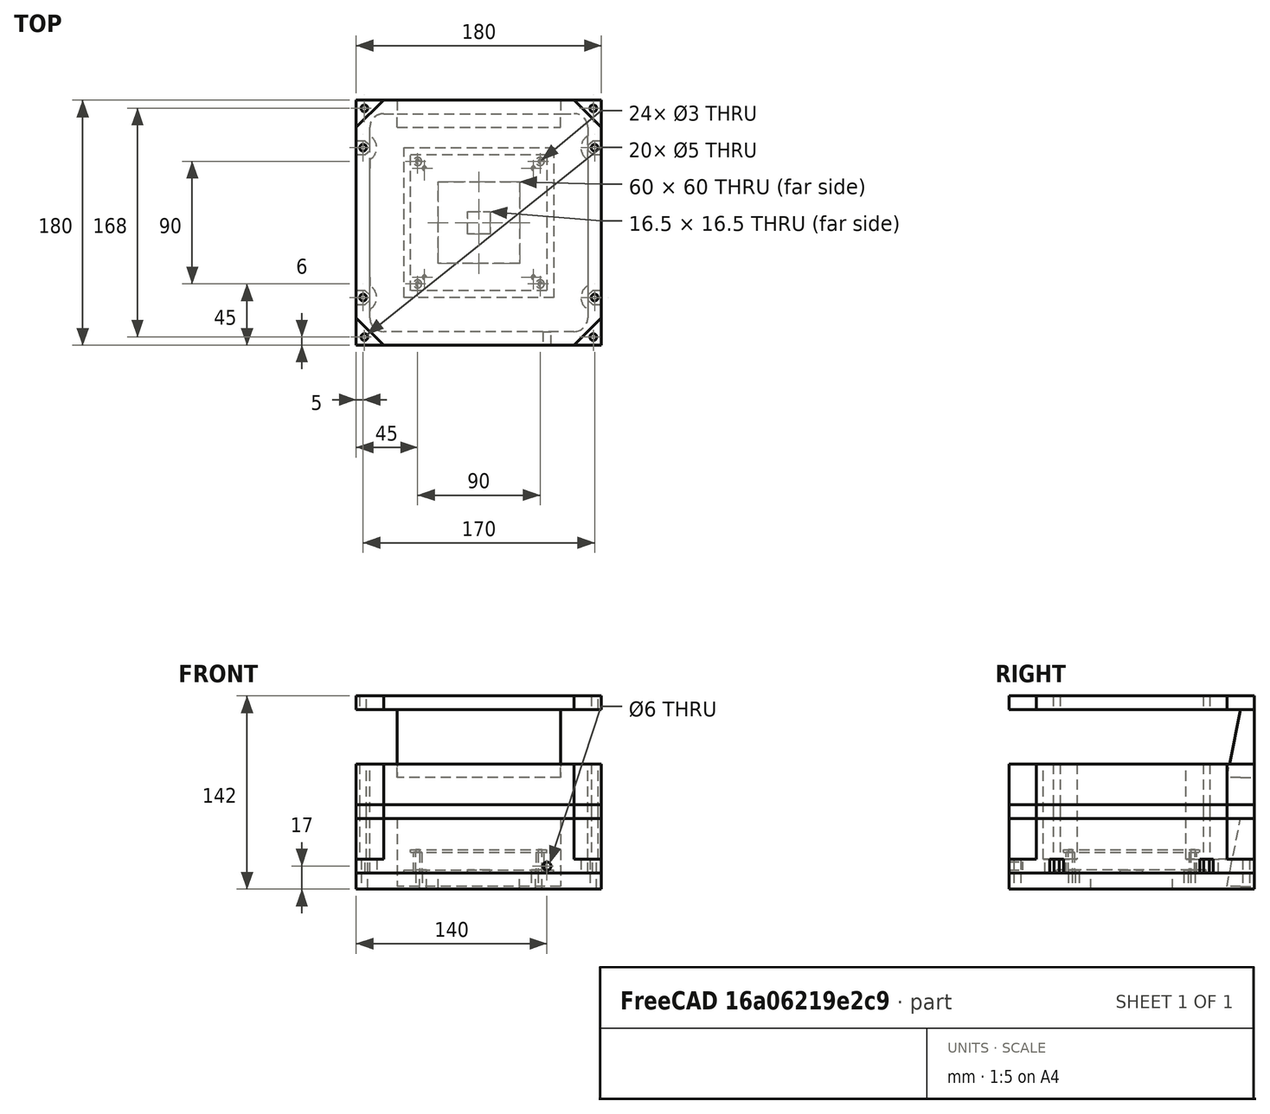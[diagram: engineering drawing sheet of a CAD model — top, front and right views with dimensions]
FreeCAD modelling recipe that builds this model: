
FCSTD DOCUMENT  (FreeCAD 0.19R24291 (Git))
Label: Cooling_skizze_1
License: All rights reserved
LicenseURL: http://en.wikipedia.org/wiki/All_rights_reserved
objects: TechDraw::DrawViewDimension×33, Sketcher::SketchObject×14, PartDesign::Pad×7, PartDesign::Pocket×6, PartDesign::Body×5, TechDraw::DrawViewAnnotation×4, PartDesign::PolarPattern×3, TechDraw::DrawSVGTemplate×3, TechDraw::DrawViewPart×3, TechDraw::DrawPage×3, PartDesign::AdditiveWedge×1, Part::Fuse×1
note: 51 computed .brp shape members not serialized (recipe doc carries the construction recipe); baked Part::Feature solids carry a one-line shape summary decoded from their .brp

FEATURE [Sketcher::SketchObject] Sketch  label="Sides"
  FullyConstrained = true
  MapMode = 2
  Support = -> [Sketch]
  sketch-geometry (31):
    g0: LineSegment StartX=-90 StartY=90 StartZ=0 EndX=90 EndY=90 EndZ=0
    g1: LineSegment StartX=90 StartY=90 StartZ=0 EndX=90 EndY=-90 EndZ=0
    g2: LineSegment StartX=90 StartY=-90 StartZ=0 EndX=-90 EndY=-90 EndZ=0
    g3: LineSegment StartX=-90 StartY=-90 StartZ=0 EndX=-90 EndY=90 EndZ=0
    g4: LineSegment StartX=-70 StartY=80 StartZ=0 EndX=70 EndY=80 EndZ=0
    g5: LineSegment StartX=80 StartY=70 StartZ=0 EndX=80 EndY=63.6603 EndZ=0
    g6: LineSegment StartX=70 StartY=-80 StartZ=0 EndX=-70 EndY=-80 EndZ=0
    g7: LineSegment StartX=-80 StartY=-70 StartZ=0 EndX=-80 EndY=-63.6603 EndZ=0
    g8: ArcOfCircle CenterX=70 CenterY=70 CenterZ=0 NormalX=0 NormalY=0 NormalZ=1 AngleXU=0 Radius=10 StartAngle=2.1e-15 EndAngle=1.5708
    g9: ArcOfCircle CenterX=70 CenterY=-70 CenterZ=0 NormalX=0 NormalY=0 NormalZ=1 AngleXU=0 Radius=10 StartAngle=4.71239 EndAngle=6.28319
    g10: GeomPoint X=80 Y=-80 Z=0
    g11: ArcOfCircle CenterX=-70 CenterY=-70 CenterZ=0 NormalX=0 NormalY=0 NormalZ=1 AngleXU=0 Radius=10 StartAngle=3.14159 EndAngle=4.71239
    g12: GeomPoint X=-80 Y=-80 Z=0
    g13: ArcOfCircle CenterX=-70 CenterY=70 CenterZ=0 NormalX=0 NormalY=0 NormalZ=1 AngleXU=0 Radius=10 StartAngle=1.5708 EndAngle=3.14212
    g14: GeomPoint X=-80 Y=80 Z=0
    g15: ArcOfCircle CenterX=-85 CenterY=55 CenterZ=0 NormalX=0 NormalY=0 NormalZ=1 AngleXU=0 Radius=10 StartAngle=5.23599 EndAngle=7.33038
    g16: LineSegment StartX=-80 StartY=63.6603 StartZ=0 EndX=-80 EndY=69.9948 EndZ=0
    g17: ArcOfCircle CenterX=85 CenterY=55 CenterZ=0 NormalX=0 NormalY=0 NormalZ=1 AngleXU=0 Radius=10 StartAngle=2.0944 EndAngle=4.18879
    g18: LineSegment StartX=80 StartY=46.3397 StartZ=0 EndX=80 EndY=-46.3397 EndZ=0
    g19: ArcOfCircle CenterX=-85 CenterY=-55 CenterZ=0 NormalX=0 NormalY=0 NormalZ=1 AngleXU=0 Radius=10 StartAngle=5.23599 EndAngle=7.33038
    g20: LineSegment StartX=-80 StartY=-46.3397 StartZ=0 EndX=-80 EndY=46.3397 EndZ=0
    g21: ArcOfCircle CenterX=85 CenterY=-55 CenterZ=0 NormalX=0 NormalY=0 NormalZ=1 AngleXU=0 Radius=10 StartAngle=2.0944 EndAngle=4.18879
    g22: LineSegment StartX=80 StartY=-63.6603 StartZ=0 EndX=80 EndY=-70 EndZ=0
    g23: Circle CenterX=-84 CenterY=84 CenterZ=0 NormalX=0 NormalY=0 NormalZ=1 AngleXU=0 Radius=2.5
    g24: Circle CenterX=84 CenterY=84 CenterZ=0 NormalX=0 NormalY=0 NormalZ=1 AngleXU=0 Radius=2.5
    g25: Circle CenterX=84 CenterY=-84 CenterZ=0 NormalX=0 NormalY=0 NormalZ=1 AngleXU=0 Radius=2.5
    g26: Circle CenterX=-84 CenterY=-84 CenterZ=0 NormalX=0 NormalY=0 NormalZ=1 AngleXU=0 Radius=2.5
    g27: Circle CenterX=-85 CenterY=55 CenterZ=0 NormalX=0 NormalY=0 NormalZ=1 AngleXU=0 Radius=2.5
    g28: Circle CenterX=-85 CenterY=-55 CenterZ=0 NormalX=0 NormalY=0 NormalZ=1 AngleXU=0 Radius=2.5
    g29: Circle CenterX=85 CenterY=-55 CenterZ=0 NormalX=0 NormalY=0 NormalZ=1 AngleXU=0 Radius=2.5
    g30: Circle CenterX=85 CenterY=55 CenterZ=0 NormalX=0 NormalY=0 NormalZ=1 AngleXU=0 Radius=2.5
  constraints (85):
    c: Coincident(g0,g1)
    c: Coincident(g1,g2)
    c: Coincident(g2,g3)
    c: Coincident(g3,g0)
    c: Horizontal(g0)
    c: Horizontal(g2)
    c: Vertical(g1)
    c: Vertical(g3)
    c: Horizontal(g6)
    c: Vertical(g7)
    c: Distance(g0) = 180
    c: Distance(g1) = 180
    c: Distance(g12,g10) = 160
    c: Distance(g14,g12) = 160
    c: Tangent(g5,g8) = 1.5708
    c: Tangent(g4,g8) = 1.5708
    c: PointOnObject(g10,g5)
    c: PointOnObject(g10,g6)
    c: Coincident(g22,g9) = 1.5708
    c: Tangent(g6,g9) = 1.5708
    c: PointOnObject(g12,g6)
    c: Tangent(g6,g11) = 1.5708
    c: Tangent(g7,g11) = 1.5708
    c: PointOnObject(g14,g7)
    c: PointOnObject(g14,g4)
    c: Coincident(g16,g13) = 1.5708
    c: Tangent(g4,g13) = 1.5708
    c: Radius(g11) = 10
    c: Coincident(g16,g15)
    c: Tangent(g7,g16)
    c: Coincident(g20,g15)
    c: Tangent(g5,g18)
    c: Coincident(g5,g17)
    c: Coincident(g20,g19)
    c: Tangent(g7,g20)
    c: Coincident(g7,g19)
    c: PointOnObject(g21,g18)
    c: Coincident(g18,g21)
    c: Coincident(g17,g18)
    c: Coincident(g21,g22)
    c: Radius(g9) = 10
    c: Radius(g19) = 10
    c: Radius(g15) = 10
    c: Diameter(g23) = 5  'Bohrung 1-b'
    c: DistanceY(g23,g0) = 6  'Versatz_y1-b'
    c: Diameter(g24) = 5  'Bohrung 2-b'
    c: DistanceX(g24,g0) = 6  'Versatz_x2-b'
    c: DistanceY(g24,g0) = 6  'Versatz_y2-b'
    c: DistanceX(g0,g23) = 6  'Versatz_x1-b'
    c: DistanceX(g8,g0) = 20
    c: DistanceY(g8,g0) = 20
    c: Diameter(g25) = 5  'Bohrung 3-b'
    c: DistanceX(g25,g1) = 6  'Versatz_x3-b'
    c: DistanceY(g1,g25) = 6  'Versatz_y3-b'
    c: Diameter(g26) = 5  'Bohrung 4-b'
    c: DistanceX(g2,g26) = 6  'Versatz_x4-b'
    c: DistanceY(g2,g26) = 6  'Versatz_y4-b'
    c: Coincident(g27,g15)
    c: Diameter(g27) = 5  'Bohrung 1-t'
    c: Coincident(g28,g19)
    c: Diameter(g28) = 5  'Bohrung 4-t'
    c: Coincident(g29,g21)
    c: Diameter(g29) = 5  'Bohrung 3-t'
    c: Coincident(g30,g17)
    c: Diameter(g30) = 5  'Bohrung 2-t'
    c: DistanceY(g15,g23) = 29  'Abstand 1b-t'
    c: DistanceX(g0,g15) = 5  'Versatz_1-t'
    c: Radius(g17) = 10
    c: DistanceY(g17,g24) = 29  'Abstand 2b-t'
    c: DistanceX(g17,g0) = 5  'Versatz_2-t'
    c: Radius(g21) = 10
    c: DistanceY(g25,g21) = 29  'Abstand 3b-t'
    c: DistanceX(g21,g1) = 5  'Versatz_3-t'
    c: DistanceY(g26,g19) = 29  'Abstand 4b-t'
    c: DistanceX(g2,g19) = 5  'Versatz_4-t'
    c: DistanceX(g0,g-1) = 90
    c: DistanceY(g-1,g0) = 90
    c: DistanceX(g-1,g10) = 80
    c: DistanceY(g10,g-1) = 80
    c: DistanceY(g10,g14) = 160
    c: DistanceX(g12,g4) = 150
    c: DistanceX(g4,g4) = 140
    c: Distance(g6) = 140
    c: DistanceY(g6,g9) = 10
    c: DistanceY(g13,g14) = 10
FEATURE [PartDesign::Pad] Pad  label="Bodypad"
  Direction = (1,1,1)
  Length = 80
  Length2 = 100
  Profile = -> Sketch
  Type = 0
FEATURE [Sketcher::SketchObject] Sketch001  label="Side-Cutout"
  FullyConstrained = true
  MapMode = 5
  Placement = pos=(0,90,0) rot=(0,0.707107,0.707107;3.14159rad)
  Support = -> [Pad]
  sketch-geometry (4):
    g0: LineSegment StartX=-60 StartY=80 StartZ=0 EndX=60 EndY=80 EndZ=0
    g1: LineSegment StartX=60 StartY=80 StartZ=0 EndX=60 EndY=0 EndZ=0
    g2: LineSegment StartX=60 StartY=0 StartZ=0 EndX=-60 EndY=0 EndZ=0
    g3: LineSegment StartX=-60 StartY=0 StartZ=0 EndX=-60 EndY=80 EndZ=0
  constraints (12):
    c: Coincident(g0,g1)
    c: Coincident(g1,g2)
    c: Coincident(g2,g3)
    c: Coincident(g3,g0)
    c: Horizontal(g0)
    c: Horizontal(g2)
    c: Vertical(g1)
    c: Vertical(g3)
    c: Distance(g0) = 120
    c: DistanceX(g0,g-1) = 60
    c: DistanceY(g-1,g0) = 80
    c: Distance(g1) = 80
FEATURE [PartDesign::Pocket] Pocket  label="Cutout-Side"
  BaseFeature = -> Pad
  Length = 11
  Length2 = 100
  Profile = -> Sketch001
  Type = 0
FEATURE [Sketcher::SketchObject] Sketch003  label="Cutdown B"
  FullyConstrained = true
  MapMode = 5
  Placement = pos=(0,0,80) rot=(0,0,1;0rad)
  sketch-geometry (3):
    g0: LineSegment StartX=-90 StartY=90 StartZ=0 EndX=-70 EndY=90 EndZ=0
    g1: LineSegment StartX=-90 StartY=70 StartZ=0 EndX=-90 EndY=90 EndZ=0
    g2: LineSegment StartX=-90 StartY=70 StartZ=0 EndX=-70 EndY=90 EndZ=0
  constraints (9):
    c: Coincident(g1,g0)
    c: Horizontal(g0)
    c: Vertical(g1)
    c: DistanceX(g0,g-1) = 90
    c: DistanceY(g-1,g0) = 90
    c: Distance(g0) = 20
    c: PointOnObject(g2,g0)
    c: Block(g2)
    c: Distance(g1) = 20
FEATURE [PartDesign::Pocket] Pocket002  label="Cut-Down B"
  BaseFeature = -> Pocket
  Length = 70
  Length2 = 100
  Profile = -> Sketch003
  Type = 0
FEATURE [PartDesign::PolarPattern] PolarPattern  label="PatternCutDownsB"
  Angle = 360
  Axis = -> Sketch003 [N_Axis]
  BaseFeature = -> Pocket002
  Occurrences = 4
  Originals = -> [Pocket002]
FEATURE [Sketcher::SketchObject] Sketch004  label="Cutdown T"
  FullyConstrained = true
  MapMode = 5
  Placement = pos=(0,0,0) rot=(1,0,0;3.14159rad)
  Support = -> [PolarPattern]
  sketch-geometry (24):
    g0: LineSegment StartX=-90 StartY=60 StartZ=0 EndX=-83.5 EndY=60 EndZ=0
    g1: LineSegment StartX=-80 StartY=57 StartZ=0 EndX=-80 EndY=53 EndZ=0
    g2: LineSegment StartX=-83.5 StartY=50 StartZ=0 EndX=-90 EndY=50 EndZ=0
    g3: LineSegment StartX=-90 StartY=50 StartZ=0 EndX=-90 EndY=60 EndZ=0
    g4: LineSegment StartX=83.5 StartY=60 StartZ=0 EndX=90 EndY=60 EndZ=0
    g5: LineSegment StartX=90 StartY=60 StartZ=0 EndX=90 EndY=50 EndZ=0
    g6: LineSegment StartX=90 StartY=50 StartZ=0 EndX=83.5 EndY=50 EndZ=0
    g7: LineSegment StartX=80 StartY=53 StartZ=0 EndX=80 EndY=57 EndZ=0
    g8: LineSegment StartX=83.5 StartY=-50 StartZ=0 EndX=90 EndY=-50 EndZ=0
    g9: LineSegment StartX=90 StartY=-50 StartZ=0 EndX=90 EndY=-60 EndZ=0
    g10: LineSegment StartX=90 StartY=-60 StartZ=0 EndX=83.5 EndY=-60 EndZ=0
    g11: LineSegment StartX=80 StartY=-57 StartZ=0 EndX=80 EndY=-53 EndZ=0
    g12: LineSegment StartX=-90 StartY=-50 StartZ=0 EndX=-83.5 EndY=-50 EndZ=0
    g13: LineSegment StartX=-80 StartY=-53 StartZ=0 EndX=-80 EndY=-57 EndZ=0
    g14: LineSegment StartX=-83.5 StartY=-60 StartZ=0 EndX=-90 EndY=-60 EndZ=0
    g15: LineSegment StartX=-90 StartY=-60 StartZ=0 EndX=-90 EndY=-50 EndZ=0
    g16: LineSegment StartX=-83.5 StartY=-50 StartZ=0 EndX=-80 EndY=-53 EndZ=0
    g17: LineSegment StartX=-83.5 StartY=-60 StartZ=0 EndX=-80 EndY=-57 EndZ=0
    g18: LineSegment StartX=-83.5 StartY=60 StartZ=0 EndX=-80 EndY=57 EndZ=0
    g19: LineSegment StartX=-80 StartY=53 StartZ=0 EndX=-83.5 EndY=50 EndZ=0
    g20: LineSegment StartX=83.5 StartY=-50 StartZ=0 EndX=80 EndY=-53 EndZ=0
    g21: LineSegment StartX=80 StartY=-57 StartZ=0 EndX=83.5 EndY=-60 EndZ=0
    g22: LineSegment StartX=83.5 StartY=60 StartZ=0 EndX=80 EndY=57 EndZ=0
    g23: LineSegment StartX=80 StartY=53 StartZ=0 EndX=83.5 EndY=50 EndZ=0
  constraints (72):
    c: Coincident(g2,g3)
    c: Coincident(g3,g0)
    c: Horizontal(g0)
    c: Horizontal(g2)
    c: Vertical(g1)
    c: Vertical(g3)
    c: Distance(g3) = 10
    c: DistanceX(g0,g-1) = 90
    c: DistanceY(g-1,g0) = 60
    c: Coincident(g4,g5)
    c: Coincident(g5,g6)
    c: Horizontal(g4)
    c: Horizontal(g6)
    c: Vertical(g5)
    c: Vertical(g7)
    c: Coincident(g8,g9)
    c: Coincident(g9,g10)
    c: Horizontal(g8)
    c: Horizontal(g10)
    c: Vertical(g9)
    c: Vertical(g11)
    c: Coincident(g14,g15)
    c: Coincident(g15,g12)
    c: Horizontal(g12)
    c: Horizontal(g14)
    c: Vertical(g13)
    c: Vertical(g15)
    c: Distance(g5) = 10
    c: Distance(g9) = 10
    c: DistanceX(g14,g-1) = 90
    c: DistanceY(g14,g-1) = 60
    c: DistanceY(g9,g-1) = 60
    c: DistanceX(g-1,g9) = 90
    c: DistanceY(g-1,g4) = 60
    c: DistanceX(g-1,g4) = 90
    c: DistanceX(g12,g16) = 6.5
    c: DistanceX(g14,g17) = 6.5
    c: Coincident(g13,g17)
    c: Coincident(g14,g17)
    c: Coincident(g13,g16)
    c: Coincident(g12,g16)
    c: DistanceX(g2,g19) = 6.5
    c: DistanceX(g0,g18) = 6.5
    c: Block(g19)
    c: Coincident(g1,g18)
    c: Coincident(g0,g18)
    c: Coincident(g1,g19)
    c: PointOnObject(g2,g19)
    c: Distance(g1) = 4
    c: Distance(g13) = 4
    c: Distance(g15) = 10
    c: DistanceX(g12,g13) = 3.5
    c: Coincident(g8,g20)
    c: Coincident(g11,g20)
    c: Coincident(g11,g21)
    c: Distance(g10) = 6.5
    c: Coincident(g10,g21)
    c: Distance(g8) = 6.5
    c: Distance(g11) = 4
    c: DistanceX(g11,g8) = 10
    c: Coincident(g4,g22)
    c: Coincident(g7,g22)
    c: Coincident(g7,g23)
    c: Coincident(g6,g23)
    c: Distance(g7) = 4
    c: Distance(g4) = 6.5
    c: Distance(g6) = 6.5
    c: DistanceX(g7,g4) = 10
    c: DistanceY(g11,g8) = 3
    c: DistanceY(g7,g4) = 3
    c: DistanceY(g1,g0) = 3
    c: DistanceY(g13,g12) = 3
FEATURE [PartDesign::Pocket] Pocket003
  BaseFeature = -> PolarPattern
  Length = 10
  Length2 = 100
  Profile = -> Sketch004
  Type = 0
FEATURE [Sketcher::SketchObject] Sketch005  label="Cutdown Bulge"
  FullyConstrained = true
  MapMode = 5
  Placement = pos=(0,0,10) rot=(0,0,1;0rad)
  Support = -> [Pocket003]
  sketch-geometry (16):
    g0: LineSegment StartX=-80 StartY=70 StartZ=0 EndX=-70 EndY=70 EndZ=0
    g1: LineSegment StartX=-70 StartY=70 StartZ=0 EndX=-70 EndY=40 EndZ=0
    g2: LineSegment StartX=-70 StartY=40 StartZ=0 EndX=-80 EndY=40 EndZ=0
    g3: LineSegment StartX=-80 StartY=40 StartZ=0 EndX=-80 EndY=70 EndZ=0
    g4: LineSegment StartX=80 StartY=70 StartZ=0 EndX=70 EndY=70 EndZ=0
    g5: LineSegment StartX=70 StartY=70 StartZ=0 EndX=70 EndY=40 EndZ=0
    g6: LineSegment StartX=70 StartY=40 StartZ=0 EndX=80 EndY=40 EndZ=0
    g7: LineSegment StartX=80 StartY=40 StartZ=0 EndX=80 EndY=70 EndZ=0
    g8: LineSegment StartX=70 StartY=-40 StartZ=0 EndX=80 EndY=-40 EndZ=0
    g9: LineSegment StartX=80 StartY=-40 StartZ=0 EndX=80 EndY=-70 EndZ=0
    g10: LineSegment StartX=80 StartY=-70 StartZ=0 EndX=70 EndY=-70 EndZ=0
    g11: LineSegment StartX=70 StartY=-70 StartZ=0 EndX=70 EndY=-40 EndZ=0
    g12: LineSegment StartX=-70 StartY=-65 StartZ=0 EndX=-80 EndY=-65 EndZ=0
    g13: LineSegment StartX=-80 StartY=-65 StartZ=0 EndX=-80 EndY=-40 EndZ=0
    g14: LineSegment StartX=-80 StartY=-40 StartZ=0 EndX=-70 EndY=-40 EndZ=0
    g15: LineSegment StartX=-70 StartY=-40 StartZ=0 EndX=-70 EndY=-65 EndZ=0
  constraints (48):
    c: Coincident(g0,g1)
    c: Coincident(g1,g2)
    c: Coincident(g2,g3)
    c: Coincident(g3,g0)
    c: Horizontal(g0)
    c: Horizontal(g2)
    c: Vertical(g1)
    c: Vertical(g3)
    c: Distance(g0) = 10
    c: Distance(g1) = 30
    c: DistanceY(g-1,g0) = 70
    c: DistanceX(g0,g-1) = 80
    c: Coincident(g4,g5)
    c: Coincident(g5,g6)
    c: Coincident(g6,g7)
    c: Coincident(g7,g4)
    c: Horizontal(g4)
    c: Horizontal(g6)
    c: Vertical(g5)
    c: Vertical(g7)
    c: Coincident(g8,g9)
    c: Coincident(g9,g10)
    c: Coincident(g10,g11)
    c: Coincident(g11,g8)
    c: Horizontal(g8)
    c: Horizontal(g10)
    c: Vertical(g9)
    c: Vertical(g11)
    c: Coincident(g12,g13)
    c: Coincident(g13,g14)
    c: Coincident(g14,g15)
    c: Coincident(g15,g12)
    c: Horizontal(g12)
    c: Horizontal(g14)
    c: Vertical(g13)
    c: Vertical(g15)
    c: Distance(g15) = 25
    c: Distance(g11) = 30
    c: Distance(g5) = 30
    c: Distance(g6) = 10
    c: Distance(g8) = 10
    c: Distance(g14) = 10
    c: DistanceX(g14,g-1) = 70
    c: DistanceY(g14,g-1) = 40
    c: DistanceY(g8,g-1) = 40
    c: DistanceX(g-1,g8) = 70
    c: DistanceX(g-1,g5) = 70
    c: DistanceY(g-1,g5) = 40
FEATURE [PartDesign::Pocket] Pocket004
  BaseFeature = -> Pocket003
  Length = 70
  Length2 = 100
  Profile = -> Sketch005
  Reversed = true
  Type = 0
FEATURE [Sketcher::SketchObject] Sketch002  label="N2-Loch"
  FullyConstrained = true
  MapMode = 5
  Placement = pos=(0,-80,0) rot=(0,0.707107,0.707107;3.14159rad)
  Support = -> [Pocket004]
  sketch-geometry (1):
    g0: Circle CenterX=-50 CenterY=5 CenterZ=0 NormalX=0 NormalY=0 NormalZ=1 AngleXU=0 Radius=3
  constraints (3):
    c: Diameter(g0) = 6
    c: DistanceX(g0,g-1) = 50
    c: DistanceY(g-1,g0) = 5
FEATURE [Sketcher::SketchObject] Sketch006  label="Alu-Baseplate001"
  FullyConstrained = true
  MapMode = 2
  sketch-geometry (20):
    g0: LineSegment StartX=-90 StartY=90 StartZ=0 EndX=90 EndY=90 EndZ=0
    g1: LineSegment StartX=90 StartY=90 StartZ=0 EndX=90 EndY=-90 EndZ=0
    g2: LineSegment StartX=90 StartY=-90 StartZ=0 EndX=-90 EndY=-90 EndZ=0
    g3: LineSegment StartX=-90 StartY=-90 StartZ=0 EndX=-90 EndY=90 EndZ=0
    g4: LineSegment StartX=-30 StartY=30 StartZ=0 EndX=30 EndY=30 EndZ=0
    g5: LineSegment StartX=30 StartY=30 StartZ=0 EndX=30 EndY=-30 EndZ=0
    g6: LineSegment StartX=30 StartY=-30 StartZ=0 EndX=-30 EndY=-30 EndZ=0
    g7: LineSegment StartX=-30 StartY=-30 StartZ=0 EndX=-30 EndY=30 EndZ=0
    g8: Circle CenterX=40 CenterY=40 CenterZ=0 NormalX=0 NormalY=0 NormalZ=1 AngleXU=0 Radius=1.5
    g9: Circle CenterX=40 CenterY=-40 CenterZ=0 NormalX=0 NormalY=0 NormalZ=1 AngleXU=0 Radius=1.5
    g10: Circle CenterX=-40 CenterY=-40 CenterZ=0 NormalX=0 NormalY=0 NormalZ=1 AngleXU=0 Radius=1.5
    g11: Circle CenterX=-40 CenterY=40 CenterZ=0 NormalX=0 NormalY=0 NormalZ=1 AngleXU=0 Radius=1.5
    g12: Circle CenterX=-45 CenterY=45 CenterZ=0 NormalX=0 NormalY=0 NormalZ=1 AngleXU=0 Radius=1.5
    g13: Circle CenterX=45 CenterY=45 CenterZ=0 NormalX=0 NormalY=0 NormalZ=1 AngleXU=0 Radius=1.5
    g14: Circle CenterX=45 CenterY=-45 CenterZ=0 NormalX=0 NormalY=0 NormalZ=1 AngleXU=0 Radius=1.5
    g15: Circle CenterX=-45 CenterY=-45 CenterZ=0 NormalX=0 NormalY=0 NormalZ=1 AngleXU=0 Radius=1.5
    g16: Circle CenterX=-84 CenterY=84 CenterZ=0 NormalX=0 NormalY=0 NormalZ=1 AngleXU=0 Radius=2.5
    g17: Circle CenterX=84 CenterY=84 CenterZ=0 NormalX=0 NormalY=0 NormalZ=1 AngleXU=0 Radius=2.5
    g18: Circle CenterX=84 CenterY=-84 CenterZ=0 NormalX=0 NormalY=0 NormalZ=1 AngleXU=0 Radius=2.5
    g19: Circle CenterX=-84 CenterY=-84 CenterZ=0 NormalX=0 NormalY=0 NormalZ=1 AngleXU=0 Radius=2.5
  constraints (60):
    c: Coincident(g0,g1)
    c: Coincident(g1,g2)
    c: Coincident(g2,g3)
    c: Coincident(g3,g0)
    c: Horizontal(g0)
    c: Horizontal(g2)
    c: Vertical(g1)
    c: Vertical(g3)
    c: Distance(g0) = 180
    c: Distance(g1) = 180
    c: DistanceX(g0,g-1) = 90
    c: DistanceY(g-1,g0) = 90
    c: Coincident(g4,g5)
    c: Coincident(g5,g6)
    c: Coincident(g6,g7)
    c: Coincident(g7,g4)
    c: Horizontal(g4)
    c: Horizontal(g6)
    c: Vertical(g5)
    c: Vertical(g7)
    c: Distance(g7) = 60
    c: Distance(g4) = 60
    c: DistanceX(g4,g-1) = 30
    c: DistanceY(g-1,g4) = 30
    c: Diameter(g8) = 3
    c: Diameter(g9) = 3
    c: Diameter(g10) = 3
    c: Diameter(g11) = 3
    c: DistanceX(g11,g-1) = 40
    c: DistanceY(g-1,g11) = 40
    c: DistanceY(g10,g-1) = 40
    c: DistanceX(g10,g-1) = 40
    c: DistanceY(g9,g-1) = 40
    c: DistanceX(g-1,g9) = 40
    c: DistanceY(g-1,g8) = 40
    c: DistanceX(g-1,g8) = 40
    c: Diameter(g12) = 3
    c: Diameter(g13) = 3
    c: Diameter(g14) = 3
    c: Diameter(g15) = 3
    c: DistanceY(g15,g10) = 5
    c: DistanceX(g15,g10) = 5
    c: DistanceY(g14,g9) = 5
    c: DistanceX(g9,g14) = 5
    c: DistanceX(g8,g13) = 5
    c: DistanceY(g8,g13) = 5
    c: DistanceY(g11,g12) = 5
    c: DistanceX(g12,g11) = 5
    c: DistanceY(g16,g0) = 6
    c: DistanceX(g0,g16) = 6
    c: Diameter(g16) = 5
    c: DistanceX(g17,g0) = 6
    c: DistanceY(g17,g0) = 6
    c: Diameter(g17) = 5
    c: DistanceY(g1,g18) = 6
    c: DistanceX(g18,g1) = 6
    c: Diameter(g18) = 5
    c: DistanceY(g2,g19) = 6
    c: DistanceX(g2,g19) = 6
    c: Diameter(g19) = 5
FEATURE [PartDesign::Pad] Pad001
  Direction = (1,1,1)
  Length = 12
  Length2 = 100
  Profile = -> Sketch006
  Type = 0
FEATURE [Sketcher::SketchObject] Sketch007
  FullyConstrained = true
  MapMode = 5
  Placement = pos=(0,0,0) rot=(1,0,0;3.14159rad)
  Support = -> [Pad001]
  sketch-geometry (4):
    g0: LineSegment StartX=30 StartY=-28 StartZ=0 EndX=60 EndY=-28 EndZ=0
    g1: LineSegment StartX=60 StartY=-28 StartZ=0 EndX=60 EndY=28 EndZ=0
    g2: LineSegment StartX=60 StartY=28 StartZ=0 EndX=30 EndY=28 EndZ=0
    g3: LineSegment StartX=30 StartY=28 StartZ=0 EndX=30 EndY=-28 EndZ=0
  constraints (12):
    c: Coincident(g0,g1)
    c: Coincident(g1,g2)
    c: Coincident(g2,g3)
    c: Coincident(g3,g0)
    c: Horizontal(g0)
    c: Horizontal(g2)
    c: Vertical(g1)
    c: Vertical(g3)
    c: Distance(g0) = 30
    c: Distance(g1) = 56
    c: DistanceY(g-1,g2) = 28
    c: DistanceX(g-1,g2) = 30
FEATURE [PartDesign::Body] Body001  label="Alu-Baseplate"
  Group = -> [Sketch006,Pad001,Sketch007]
  Origin = -> Origin002
  Placement = pos=(0,0,-12) rot=(0,0,1;0rad)
  Tip = -> Pad001
FEATURE [Sketcher::SketchObject] Sketch008
  FullyConstrained = true
  sketch-geometry (8):
    g0: LineSegment StartX=-50 StartY=50 StartZ=0 EndX=50 EndY=50 EndZ=0
    g1: LineSegment StartX=50 StartY=50 StartZ=0 EndX=50 EndY=-50 EndZ=0
    g2: LineSegment StartX=50 StartY=-50 StartZ=0 EndX=-50 EndY=-50 EndZ=0
    g3: LineSegment StartX=-50 StartY=-50 StartZ=0 EndX=-50 EndY=50 EndZ=0
    g4: Circle CenterX=-45 CenterY=45 CenterZ=0 NormalX=0 NormalY=0 NormalZ=1 AngleXU=0 Radius=1.5
    g5: Circle CenterX=45 CenterY=45 CenterZ=0 NormalX=0 NormalY=0 NormalZ=1 AngleXU=0 Radius=1.5
    g6: Circle CenterX=45 CenterY=-45 CenterZ=0 NormalX=0 NormalY=0 NormalZ=1 AngleXU=0 Radius=1.5
    g7: Circle CenterX=-45 CenterY=-45 CenterZ=0 NormalX=0 NormalY=0 NormalZ=1 AngleXU=0 Radius=1.5
  constraints (24):
    c: Coincident(g0,g1)
    c: Coincident(g1,g2)
    c: Coincident(g2,g3)
    c: Coincident(g3,g0)
    c: Horizontal(g0)
    c: Horizontal(g2)
    c: Vertical(g1)
    c: Vertical(g3)
    c: Distance(g0) = 100
    c: Distance(g1) = 100
    c: DistanceX(g0,g-1) = 50
    c: DistanceY(g-1,g0) = 50
    c: DistanceX(g0,g4) = 5
    c: DistanceY(g4,g0) = 5
    c: Diameter(g4) = 3
    c: DistanceY(g5,g0) = 5
    c: DistanceX(g5,g0) = 5
    c: Diameter(g5) = 3
    c: DistanceY(g1,g6) = 5
    c: DistanceX(g6,g1) = 5
    c: Diameter(g6) = 3
    c: DistanceY(g2,g7) = 5
    c: DistanceX(g2,g7) = 5
    c: Diameter(g7) = 3
FEATURE [PartDesign::Pad] Pad002
  Direction = (1,1,1)
  Length = 2
  Length2 = 100
  Profile = -> Sketch008
  Type = 0
FEATURE [Sketcher::SketchObject] Sketch009
  FullyConstrained = true
  MapMode = 5
  Support = -> [XY_Plane003]
  sketch-geometry (2):
    g0: Circle CenterX=-45 CenterY=45 CenterZ=0 NormalX=0 NormalY=0 NormalZ=1 AngleXU=0 Radius=3
    g1: Circle CenterX=-45 CenterY=45 CenterZ=0 NormalX=0 NormalY=0 NormalZ=1 AngleXU=0 Radius=1.5
  constraints (5):
    c: DistanceY(g-1,g0) = 45
    c: DistanceX(g0,g-1) = 45
    c: Diameter(g0) = 6
    c: Coincident(g1,g0)
    c: Diameter(g1) = 3
FEATURE [PartDesign::Pad] Pad003
  BaseFeature = -> Pad002
  Direction = (0,0,-1)
  Length = 15
  Length2 = 100
  Profile = -> Sketch009
  Type = 0
  UseCustomVector = true
FEATURE [PartDesign::PolarPattern] PolarPattern001
  Angle = 360
  Axis = -> Sketch009 [N_Axis]
  BaseFeature = -> Pad003
  Occurrences = 4
  Originals = -> [Pad003]
FEATURE [PartDesign::Body] Body002  label="PCB-Mockup"
  Group = -> [Sketch008,Pad002,Sketch009,Pad003,PolarPattern001]
  Origin = -> Origin003
  Placement = pos=(0,0,15) rot=(0,0,1;0rad)
  Tip = -> PolarPattern001
FEATURE [TechDraw::DrawSVGTemplate] Template
  EditableTexts = Designed_by_Name=Designed by Name; Drawing_number=Drawing number; FC-Date=Date; FC-SC=Scale; FC-SH=Sheet; FC-Title=Title; Subtitle=Subtitle; Weight=Weight
  Height = 210
  Orientation = 1
  Width = 297
FEATURE [Sketcher::SketchObject] Sketch010
  FullyConstrained = true
  MapMode = 5
  Support = -> [XY_Plane004]
  sketch-geometry (8):
    g0: LineSegment StartX=-90 StartY=90 StartZ=0 EndX=90 EndY=90 EndZ=0
    g1: LineSegment StartX=90 StartY=90 StartZ=0 EndX=90 EndY=-90 EndZ=0
    g2: LineSegment StartX=90 StartY=-90 StartZ=0 EndX=-90 EndY=-90 EndZ=0
    g3: LineSegment StartX=-90 StartY=-90 StartZ=0 EndX=-90 EndY=90 EndZ=0
    g4: Circle CenterX=-85 CenterY=55 CenterZ=0 NormalX=0 NormalY=0 NormalZ=1 AngleXU=0 Radius=2.5
    g5: Circle CenterX=85 CenterY=55 CenterZ=0 NormalX=0 NormalY=0 NormalZ=1 AngleXU=0 Radius=2.5
    g6: Circle CenterX=85 CenterY=-55 CenterZ=0 NormalX=0 NormalY=0 NormalZ=1 AngleXU=0 Radius=2.5
    g7: Circle CenterX=-85 CenterY=-55 CenterZ=0 NormalX=0 NormalY=0 NormalZ=1 AngleXU=0 Radius=2.5
  constraints (24):
    c: Coincident(g0,g1)
    c: Coincident(g1,g2)
    c: Coincident(g2,g3)
    c: Coincident(g3,g0)
    c: Horizontal(g0)
    c: Horizontal(g2)
    c: Vertical(g1)
    c: Vertical(g3)
    c: Distance(g0) = 180
    c: Distance(g1) = 180
    c: DistanceY(g-1,g0) = 90
    c: DistanceX(g0,g-1) = 90
    c: DistanceY(g4,g0) = 35
    c: DistanceX(g0,g4) = 5
    c: Diameter(g4) = 5
    c: DistanceY(g5,g0) = 35
    c: DistanceX(g5,g0) = 5
    c: Diameter(g5) = 5
    c: DistanceY(g1,g6) = 35
    c: DistanceX(g6,g1) = 5
    c: Diameter(g6) = 5
    c: DistanceY(g2,g7) = 35
    c: DistanceX(g2,g7) = 5
    c: Diameter(g7) = 5
FEATURE [PartDesign::Pad] Pad004
  Direction = (1,1,1)
  Length = 10
  Length2 = 100
  Profile = -> Sketch010
  Type = 0
FEATURE [Sketcher::SketchObject] Sketch011
  FullyConstrained = true
  MapMode = 5
  Placement = pos=(0,0,10) rot=(0,0,1;0rad)
  Support = -> [Pad004]
  sketch-geometry (3):
    g0: LineSegment StartX=-90 StartY=90 StartZ=0 EndX=-70 EndY=90 EndZ=0
    g1: LineSegment StartX=-90 StartY=90 StartZ=0 EndX=-90 EndY=70 EndZ=0
    g2: LineSegment StartX=-90 StartY=70 StartZ=0 EndX=-70 EndY=90 EndZ=0
  constraints (9):
    c: Horizontal(g0)
    c: Coincident(g1,g0)
    c: Vertical(g1)
    c: Coincident(g2,g1)
    c: Coincident(g2,g0)
    c: Distance(g0) = 20
    c: Distance(g1) = 20
    c: DistanceY(g-1,g0) = 90
    c: DistanceX(g0,g-1) = 90
FEATURE [PartDesign::Pocket] Pocket006
  BaseFeature = -> Pad004
  Length = 10
  Length2 = 100
  Profile = -> Sketch011
  Type = 0
FEATURE [PartDesign::PolarPattern] PolarPattern002
  Angle = 360
  Axis = -> Sketch011 [N_Axis]
  BaseFeature = -> Pocket006
  Occurrences = 4
  Originals = -> [Pocket006]
FEATURE [Sketcher::SketchObject] Sketch012
  FullyConstrained = true
  MapMode = 5
  Support = -> [XY_Plane004]
  sketch-geometry (4):
    g0: LineSegment StartX=-60 StartY=80 StartZ=0 EndX=60 EndY=80 EndZ=0
    g1: LineSegment StartX=60 StartY=80 StartZ=0 EndX=60 EndY=90 EndZ=0
    g2: LineSegment StartX=60 StartY=90 StartZ=0 EndX=-60 EndY=90 EndZ=0
    g3: LineSegment StartX=-60 StartY=90 StartZ=0 EndX=-60 EndY=80 EndZ=0
  constraints (12):
    c: Coincident(g0,g1)
    c: Coincident(g1,g2)
    c: Coincident(g2,g3)
    c: Coincident(g3,g0)
    c: Horizontal(g0)
    c: Horizontal(g2)
    c: Vertical(g1)
    c: Vertical(g3)
    c: Distance(g0) = 120
    c: Distance(g1) = 10
    c: DistanceY(g-1,g0) = 80
    c: DistanceX(g-1,g0) = 60
FEATURE [PartDesign::Pad] Pad005
  BaseFeature = -> PolarPattern002
  Direction = (0,0,-1)
  Length = 50
  Length2 = 100
  Profile = -> Sketch012
  Type = 0
  UseCustomVector = true
FEATURE [TechDraw::DrawViewPart] View
  CoarseView = false
  Direction = (0,0,1)
  Focus = 100
  HardHidden = false
  IsoCount = 0
  IsoHidden = false
  IsoVisible = false
  LockPosition = false
  Perspective = false
  Rotation = 0
  Scale = 0.75
  ScaleType = 0
  SeamHidden = false
  SeamVisible = true
  SmoothHidden = false
  SmoothVisible = true
  Source = -> [Pad005]
  X = 90
  XDirection = (1,0,0)
  Y = 128
FEATURE [TechDraw::DrawViewDimension] Dimension
  Arbitrary = false
  ArbitraryTolerances = false
  EqualTolerance = true
  FormatSpec = %.2f
  FormatSpecOverTolerance = %+.2f
  FormatSpecUnderTolerance = %+.2f
  Inverted = false
  LockPosition = false
  MeasureType = 1
  OverTolerance = 0
  References2D = -> [View]
  Rotation = 0
  ScaleType = 0
  TheoreticalExact = false
  Type = 1
  UnderTolerance = 0
  X = -0.341463
  Y = 62.378
FEATURE [TechDraw::DrawViewDimension] Dimension001
  Arbitrary = false
  ArbitraryTolerances = false
  EqualTolerance = true
  FormatSpec = %.2f
  FormatSpecOverTolerance = %+.2f
  FormatSpecUnderTolerance = %+.2f
  Inverted = false
  LockPosition = false
  MeasureType = 1
  OverTolerance = 0
  References2D = -> [View]
  Rotation = 0
  ScaleType = 0
  TheoreticalExact = false
  Type = 2
  UnderTolerance = 0
  X = -77.7439
  Y = 0.682927
FEATURE [TechDraw::DrawViewDimension] Dimension002
  Arbitrary = false
  ArbitraryTolerances = false
  EqualTolerance = true
  FormatSpec = %.2f
  FormatSpecOverTolerance = %+.2f
  FormatSpecUnderTolerance = %+.2f
  Inverted = false
  LockPosition = false
  MeasureType = 1
  OverTolerance = 0
  References2D = -> [View]
  Rotation = 0
  ScaleType = 0
  TheoreticalExact = false
  Type = 1
  UnderTolerance = 0
  X = 60
  Y = 60
FEATURE [TechDraw::DrawViewDimension] Dimension003
  Arbitrary = false
  ArbitraryTolerances = false
  EqualTolerance = true
  FormatSpec = %.2f
  FormatSpecOverTolerance = %+.2f
  FormatSpecUnderTolerance = %+.2f
  Inverted = false
  LockPosition = false
  MeasureType = 1
  OverTolerance = 0
  References2D = -> [View]
  Rotation = 0
  ScaleType = 0
  TheoreticalExact = false
  Type = 2
  UnderTolerance = 0
  X = -60
  Y = 60
FEATURE [TechDraw::DrawViewDimension] Dimension004
  Arbitrary = false
  ArbitraryTolerances = false
  EqualTolerance = true
  FormatSpec = ⌀%.2f
  FormatSpecOverTolerance = %+.2f
  FormatSpecUnderTolerance = %+.2f
  Inverted = false
  LockPosition = false
  MeasureType = 1
  OverTolerance = 0
  References2D = -> [View]
  Rotation = 0
  ScaleType = 0
  TheoreticalExact = false
  Type = 5
  UnderTolerance = 0
  X = -48.8349
  Y = 46.497
FEATURE [TechDraw::DrawViewDimension] Dimension006
  Arbitrary = false
  ArbitraryTolerances = false
  EqualTolerance = true
  FormatSpec = %.2f
  FormatSpecOverTolerance = %+.2f
  FormatSpecUnderTolerance = %+.2f
  Inverted = false
  LockPosition = false
  MeasureType = 1
  OverTolerance = 0
  References2D = -> [View]
  Rotation = 0
  ScaleType = 0
  TheoreticalExact = false
  Type = 1
  UnderTolerance = 0
  X = 56.5157
  Y = 26.4224
FEATURE [TechDraw::DrawViewDimension] Dimension007
  Arbitrary = false
  ArbitraryTolerances = false
  EqualTolerance = true
  FormatSpec = %.2f
  FormatSpecOverTolerance = %+.2f
  FormatSpecUnderTolerance = %+.2f
  Inverted = false
  LockPosition = false
  MeasureType = 1
  OverTolerance = 0
  References2D = -> [View]
  Rotation = 0
  ScaleType = 0
  TheoreticalExact = false
  Type = 2
  UnderTolerance = 0
  X = 73.517
  Y = 46.6245
FEATURE [TechDraw::DrawViewDimension] Dimension008
  Arbitrary = false
  ArbitraryTolerances = false
  EqualTolerance = true
  FormatSpec = ⌀%.2f
  FormatSpecOverTolerance = %+.2f
  FormatSpecUnderTolerance = %+.2f
  Inverted = false
  LockPosition = false
  MeasureType = 1
  OverTolerance = 0
  References2D = -> [View]
  Rotation = 0
  ScaleType = 0
  TheoreticalExact = false
  Type = 5
  UnderTolerance = 0
  X = -50.271
  Y = -35.8062
FEATURE [TechDraw::DrawViewDimension] Dimension009
  Arbitrary = false
  ArbitraryTolerances = false
  EqualTolerance = true
  FormatSpec = %.2f
  FormatSpecOverTolerance = %+.2f
  FormatSpecUnderTolerance = %+.2f
  Inverted = false
  LockPosition = false
  MeasureType = 1
  OverTolerance = 0
  References2D = -> [View]
  Rotation = 0
  ScaleType = 0
  TheoreticalExact = false
  Type = 2
  UnderTolerance = 0
  X = -63.75
  Y = 0
FEATURE [TechDraw::DrawPage] Page  label="Skizze_Deckel_oben"
  KeepUpdated = true
  NextBalloonIndex = 1
  ProjectionType = 0
  Template = -> Template
  Views = -> [View,Dimension,Dimension001,Dimension002,Dimension003,Dimension004,Dimension006,Dimension007,Dimension008,Dimension009]
FEATURE [PartDesign::AdditiveWedge] Wedge
  AttacherType = Attacher::AttachEngine3D
  BaseFeature = -> Pad005
  MapMode = 5
  Placement = pos=(0,80,0) rot=(1,0,0;1.5708rad)
  Support = -> [Pad005]
  X2max = 60
  X2min = -60
  Xmax = 60
  Xmin = -60
  Ymax = 0
  Ymin = -50
  Z2max = 0
  Z2min = 0
  Zmax = 10
  Zmin = 0
FEATURE [Part::Fuse] Fusion  label="Deckel_neu"
  Base = -> Pad005
  Placement = pos=(0,0,120) rot=(0,0,1;0rad)
  Tool = -> Wedge
FEATURE [PartDesign::Body] Body003  label="Deckel"
  Group = -> [Sketch010,Pad004,Sketch011,Pocket006,PolarPattern002,Sketch012,Pad005,Wedge]
  Origin = -> Origin004
  Placement = pos=(0,0,40) rot=(0,0,1;0rad)
  Tip = -> Wedge
FEATURE [PartDesign::Pocket] Pocket007
  BaseFeature = -> Pocket004
  Length = 11
  Length2 = 100
  Profile = -> Sketch002
  Type = 0
FEATURE [PartDesign::Body] Body  label="3D-Print Gehaeuse"
  Group = -> [Sketch,Pad,Sketch001,Pocket,Sketch002,Sketch003,Pocket002,PolarPattern,Sketch004,Pocket003,Sketch005,Pocket004,Pocket007]
  Origin = -> Origin
  Tip = -> Pocket007
FEATURE [Sketcher::SketchObject] Sketch013
  FullyConstrained = true
  MapMode = 5
  Support = -> [XY_Plane005]
  sketch-geometry (16):
    g0: LineSegment StartX=-55 StartY=55 StartZ=0 EndX=55 EndY=55 EndZ=0
    g1: LineSegment StartX=55 StartY=55 StartZ=0 EndX=55 EndY=-55 EndZ=0
    g2: LineSegment StartX=55 StartY=-55 StartZ=0 EndX=-55 EndY=-55 EndZ=0
    g3: LineSegment StartX=-55 StartY=-55 StartZ=0 EndX=-55 EndY=55 EndZ=0
    g4: LineSegment StartX=-8.25 StartY=8.25 StartZ=0 EndX=8.25 EndY=8.25 EndZ=0
    g5: LineSegment StartX=8.25 StartY=8.25 StartZ=0 EndX=8.25 EndY=-8.25 EndZ=0
    g6: LineSegment StartX=8.25 StartY=-8.25 StartZ=0 EndX=-8.25 EndY=-8.25 EndZ=0
    g7: LineSegment StartX=-8.25 StartY=-8.25 StartZ=0 EndX=-8.25 EndY=8.25 EndZ=0
    g8: Circle CenterX=-40 CenterY=40 CenterZ=0 NormalX=0 NormalY=0 NormalZ=1 AngleXU=0 Radius=1.5
    g9: Circle CenterX=-45 CenterY=45 CenterZ=0 NormalX=0 NormalY=0 NormalZ=1 AngleXU=0 Radius=1.5
    g10: Circle CenterX=40 CenterY=40 CenterZ=0 NormalX=0 NormalY=0 NormalZ=1 AngleXU=0 Radius=1.5
    g11: Circle CenterX=45 CenterY=45 CenterZ=0 NormalX=0 NormalY=0 NormalZ=1 AngleXU=0 Radius=1.5
    g12: Circle CenterX=40 CenterY=-40 CenterZ=0 NormalX=0 NormalY=0 NormalZ=1 AngleXU=0 Radius=1.5
    g13: Circle CenterX=45 CenterY=-45 CenterZ=0 NormalX=0 NormalY=0 NormalZ=1 AngleXU=0 Radius=1.5
    g14: Circle CenterX=-40 CenterY=-40 CenterZ=0 NormalX=0 NormalY=0 NormalZ=1 AngleXU=0 Radius=1.5
    g15: Circle CenterX=-45 CenterY=-45 CenterZ=0 NormalX=0 NormalY=0 NormalZ=1 AngleXU=0 Radius=1.5
  constraints (48):
    c: Coincident(g0,g1)
    c: Coincident(g1,g2)
    c: Coincident(g2,g3)
    c: Coincident(g3,g0)
    c: Horizontal(g0)
    c: Horizontal(g2)
    c: Vertical(g1)
    c: Vertical(g3)
    c: Distance(g0) = 110
    c: Distance(g1) = 110
    c: DistanceX(g0,g-1) = 55
    c: DistanceY(g-1,g0) = 55
    c: Coincident(g4,g5)
    c: Coincident(g5,g6)
    c: Coincident(g6,g7)
    c: Coincident(g7,g4)
    c: Horizontal(g4)
    c: Horizontal(g6)
    c: Vertical(g5)
    c: Vertical(g7)
    c: Distance(g4) = 16.5
    c: Distance(g5) = 16.5
    c: DistanceX(g4,g-1) = 8.25
    c: DistanceY(g-1,g4) = 8.25
    c: DistanceX(g8,g-1) = 40
    c: DistanceY(g-1,g8) = 40
    c: Diameter(g8) = 3
    c: Diameter(g9) = 3
    c: Diameter(g10) = 3
    c: Diameter(g11) = 3
    c: Diameter(g12) = 3
    c: Diameter(g13) = 3
    c: Diameter(g14) = 3
    c: Diameter(g15) = 3
    c: DistanceX(g9,g-1) = 45
    c: DistanceY(g-1,g9) = 45
    c: DistanceX(g-1,g10) = 40
    c: DistanceY(g-1,g10) = 40
    c: DistanceY(g-1,g11) = 45
    c: DistanceX(g-1,g11) = 45
    c: DistanceX(g-1,g12) = 40
    c: DistanceY(g12,g-1) = 40
    c: DistanceX(g-1,g13) = 45
    c: DistanceY(g13,g-1) = 45
    c: DistanceX(g14,g-1) = 40
    c: DistanceY(g14,g-1) = 40
    c: DistanceX(g15,g-1) = 45
    c: DistanceY(g15,g-1) = 45
FEATURE [PartDesign::Pad] Pad006
  Direction = (1,1,1)
  Length = 2
  Length2 = 100
  Profile = -> Sketch013
  Type = 0
FEATURE [PartDesign::Body] Body004  label="Fixierungsplatte"
  Group = -> [Sketch013,Pad006]
  Origin = -> Origin005
  Tip = -> Pad006
FEATURE [TechDraw::DrawSVGTemplate] Template001
  EditableTexts = Designed_by_Name=Henry Schumacher; FC-Date=22.10.2021; FC-SC=1:1.25; FC-Title=Baseplate
  Height = 210
  Orientation = 1
  Width = 297
FEATURE [TechDraw::DrawViewPart] View001  label="Draufsicht"
  CoarseView = false
  Direction = (0,0,1)
  Focus = 100
  HardHidden = false
  IsoCount = 0
  IsoHidden = false
  IsoVisible = false
  LockPosition = false
  Perspective = false
  Rotation = 0
  Scale = 0.75
  ScaleType = 0
  SeamHidden = false
  SeamVisible = true
  SmoothHidden = false
  SmoothVisible = true
  Source = -> [Pad001]
  X = 81.1682
  XDirection = (0,1,0)
  Y = 130.996
FEATURE [TechDraw::DrawViewDimension] Dimension010
  Arbitrary = false
  ArbitraryTolerances = false
  EqualTolerance = true
  FormatSpec = %.2f
  FormatSpecOverTolerance = %+.2f
  FormatSpecUnderTolerance = %+.2f
  Inverted = false
  LockPosition = false
  MeasureType = 1
  OverTolerance = 0
  References2D = -> [View001]
  Rotation = 0
  ScaleType = 0
  TheoreticalExact = false
  Type = 1
  UnderTolerance = 0
  X = 1.42276
  Y = 57.7778
FEATURE [TechDraw::DrawViewDimension] Dimension012
  Arbitrary = false
  ArbitraryTolerances = false
  EqualTolerance = true
  FormatSpec = %.2f
  FormatSpecOverTolerance = %+.2f
  FormatSpecUnderTolerance = %+.2f
  Inverted = false
  LockPosition = false
  MeasureType = 1
  OverTolerance = 0
  References2D = -> [View001]
  Rotation = 0
  ScaleType = 0
  TheoreticalExact = false
  Type = 1
  UnderTolerance = 0
  X = 0
  Y = 22.5
FEATURE [TechDraw::DrawViewDimension] Dimension013
  Arbitrary = false
  ArbitraryTolerances = false
  EqualTolerance = true
  FormatSpec = %.2f
  FormatSpecOverTolerance = %+.2f
  FormatSpecUnderTolerance = %+.2f
  Inverted = false
  LockPosition = false
  MeasureType = 1
  OverTolerance = 0
  References2D = -> [View001]
  Rotation = 0
  ScaleType = 0
  TheoreticalExact = false
  Type = 2
  UnderTolerance = 0
  X = -31.0366
  Y = -2.37127
FEATURE [TechDraw::DrawViewDimension] Dimension014
  Arbitrary = false
  ArbitraryTolerances = false
  EqualTolerance = true
  FormatSpec = %.2f
  FormatSpecOverTolerance = %+.2f
  FormatSpecUnderTolerance = %+.2f
  Inverted = false
  LockPosition = false
  MeasureType = 1
  OverTolerance = 0
  References2D = -> [View001]
  Rotation = 0
  ScaleType = 0
  TheoreticalExact = false
  Type = 1
  UnderTolerance = 0
  X = 0.360778
  Y = 46.3772
FEATURE [TechDraw::DrawViewDimension] Dimension015
  Arbitrary = false
  ArbitraryTolerances = false
  EqualTolerance = true
  FormatSpec = %.2f
  FormatSpecOverTolerance = %+.2f
  FormatSpecUnderTolerance = %+.2f
  Inverted = false
  LockPosition = false
  MeasureType = 1
  OverTolerance = 0
  References2D = -> [View001]
  Rotation = 0
  ScaleType = 0
  TheoreticalExact = false
  Type = 1
  UnderTolerance = 0
  X = 0.360778
  Y = 40.2822
FEATURE [TechDraw::DrawViewDimension] Dimension016
  Arbitrary = false
  ArbitraryTolerances = false
  EqualTolerance = true
  FormatSpec = %.2f
  FormatSpecOverTolerance = %+.2f
  FormatSpecUnderTolerance = %+.2f
  Inverted = false
  LockPosition = false
  MeasureType = 1
  OverTolerance = 0
  References2D = -> [View001]
  Rotation = 0
  ScaleType = 0
  TheoreticalExact = false
  Type = 1
  UnderTolerance = 0
  X = 0
  Y = -30
FEATURE [TechDraw::DrawViewDimension] Dimension017
  Arbitrary = false
  ArbitraryTolerances = false
  EqualTolerance = true
  FormatSpec = %.2f
  FormatSpecOverTolerance = %+.2f
  FormatSpecUnderTolerance = %+.2f
  Inverted = false
  LockPosition = false
  MeasureType = 1
  OverTolerance = 0
  References2D = -> [View001]
  Rotation = 0
  ScaleType = 0
  TheoreticalExact = false
  Type = 1
  UnderTolerance = 0
  X = 0.360778
  Y = -37.3578
FEATURE [TechDraw::DrawViewDimension] Dimension018
  Arbitrary = false
  ArbitraryTolerances = false
  EqualTolerance = true
  FormatSpec = %.2f
  FormatSpecOverTolerance = %+.2f
  FormatSpecUnderTolerance = %+.2f
  Inverted = false
  LockPosition = false
  MeasureType = 1
  OverTolerance = 0
  References2D = -> [View001]
  Rotation = 0
  ScaleType = 0
  TheoreticalExact = false
  Type = 2
  UnderTolerance = 0
  X = -42.0861
  Y = 0
FEATURE [TechDraw::DrawViewDimension] Dimension019
  Arbitrary = false
  ArbitraryTolerances = false
  EqualTolerance = true
  FormatSpec = %.2f
  FormatSpecOverTolerance = %+.2f
  FormatSpecUnderTolerance = %+.2f
  Inverted = false
  LockPosition = false
  MeasureType = 1
  OverTolerance = 0
  References2D = -> [View001]
  Rotation = 0
  ScaleType = 0
  TheoreticalExact = false
  Type = 2
  UnderTolerance = 0
  X = -54.3143
  Y = 3.60778
FEATURE [TechDraw::DrawViewDimension] Dimension021
  Arbitrary = false
  ArbitraryTolerances = false
  EqualTolerance = true
  FormatSpec = %.2f
  FormatSpecOverTolerance = %+.2f
  FormatSpecUnderTolerance = %+.2f
  Inverted = false
  LockPosition = false
  MeasureType = 1
  OverTolerance = 0
  References2D = -> [View001]
  Rotation = 0
  ScaleType = 0
  TheoreticalExact = false
  Type = 1
  UnderTolerance = 0
  X = 0.790425
  Y = 64.1856
FEATURE [TechDraw::DrawViewDimension] Dimension022
  Arbitrary = false
  ArbitraryTolerances = false
  EqualTolerance = true
  FormatSpec = %.2f
  FormatSpecOverTolerance = %+.2f
  FormatSpecUnderTolerance = %+.2f
  Inverted = false
  LockPosition = false
  MeasureType = 1
  OverTolerance = 0
  References2D = -> [View001]
  Rotation = 0
  ScaleType = 0
  TheoreticalExact = false
  Type = 2
  UnderTolerance = 0
  X = 81.3976
  Y = -2.68204
FEATURE [TechDraw::DrawViewDimension] Dimension023
  Arbitrary = false
  ArbitraryTolerances = false
  EqualTolerance = true
  FormatSpec = %.2f
  FormatSpecOverTolerance = %+.2f
  FormatSpecUnderTolerance = %+.2f
  Inverted = false
  LockPosition = false
  MeasureType = 1
  OverTolerance = 0
  References2D = -> [View001]
  Rotation = 0
  ScaleType = 0
  TheoreticalExact = false
  Type = 2
  UnderTolerance = 0
  X = 74.1487
  Y = -3.0151
FEATURE [TechDraw::DrawViewDimension] Dimension024
  Arbitrary = false
  ArbitraryTolerances = false
  EqualTolerance = true
  FormatSpec = %.2f
  FormatSpecOverTolerance = %+.2f
  FormatSpecUnderTolerance = %+.2f
  Inverted = false
  LockPosition = false
  MeasureType = 1
  OverTolerance = 0
  References2D = -> [View001]
  Rotation = 0
  ScaleType = 0
  TheoreticalExact = false
  Type = 2
  UnderTolerance = 0
  X = 43.5673
  Y = 26.25
FEATURE [TechDraw::DrawViewDimension] Dimension025
  Arbitrary = false
  ArbitraryTolerances = false
  EqualTolerance = true
  FormatSpec = %.2f
  FormatSpecOverTolerance = %+.2f
  FormatSpecUnderTolerance = %+.2f
  Inverted = false
  LockPosition = false
  MeasureType = 1
  OverTolerance = 0
  References2D = -> [View001]
  Rotation = 0
  ScaleType = 0
  TheoreticalExact = false
  Type = 1
  UnderTolerance = 0
  X = 41.4027
  Y = -10.8809
FEATURE [TechDraw::DrawViewAnnotation] Annotation  label="Lochmaße"
  Font = osifont
  LineSpace = 80
  LockPosition = false
  MaxWidth = -1
  Rotation = 0
  ScaleType = 0
  Text = L\xf6cher au\xdfen: 5mm Durchmesser | L\xf6cher innen: 3mm Durchmesser
  TextSize = 5
  TextStyle = 0
  X = 62.9957
  Y = 41.7917
FEATURE [TechDraw::DrawViewAnnotation] Annotation001
  Font = osifont
  LineSpace = 80
  LockPosition = false
  MaxWidth = -1
  Rotation = 0
  ScaleType = 0
  Text = Aludicke: 12mm
  TextSize = 5
  TextStyle = 0
  X = 121.485
  Y = 41.099
FEATURE [TechDraw::DrawPage] Page001  label="Aluplatte"
  KeepUpdated = true
  NextBalloonIndex = 2
  ProjectionType = 0
  Template = -> Template001
  Views = -> [View001,Dimension010,Dimension012,Dimension013,Dimension014,Dimension015,Dimension016,Dimension017,Dimension018,Dimension019,Dimension021,Dimension022,Dimension023,Dimension024,Dimension025,Annotation,Annotation001]
FEATURE [TechDraw::DrawSVGTemplate] Template002
  EditableTexts = Designed_by_Name=Henry Schumacher; FC-Date=22.10.2021; FC-SC=1:1; FC-Title=Fixierungsplatte
  Height = 210
  Orientation = 1
  Width = 297
FEATURE [TechDraw::DrawViewPart] View002
  CoarseView = false
  Direction = (0,0,1)
  Focus = 100
  HardHidden = false
  IsoCount = 0
  IsoHidden = false
  IsoVisible = false
  LockPosition = false
  Perspective = false
  Rotation = 0
  ScaleType = 0
  SeamHidden = false
  SeamVisible = true
  SmoothHidden = false
  SmoothVisible = true
  Source = -> [Pad006]
  X = 115.776
  XDirection = (0,1,0)
  Y = 128.333
FEATURE [TechDraw::DrawViewDimension] Dimension026
  Arbitrary = false
  ArbitraryTolerances = false
  EqualTolerance = true
  FormatSpec = %.2f
  FormatSpecOverTolerance = %+.2f
  FormatSpecUnderTolerance = %+.2f
  Inverted = false
  LockPosition = false
  MeasureType = 1
  OverTolerance = 0
  References2D = -> [View002]
  Rotation = 0
  ScaleType = 0
  TheoreticalExact = false
  Type = 1
  UnderTolerance = 0
  X = 1.13821
  Y = 66.0976
FEATURE [TechDraw::DrawViewDimension] Dimension027
  Arbitrary = false
  ArbitraryTolerances = false
  EqualTolerance = true
  FormatSpec = %.2f
  FormatSpecOverTolerance = %+.2f
  FormatSpecUnderTolerance = %+.2f
  Inverted = false
  LockPosition = false
  MeasureType = 1
  OverTolerance = 0
  References2D = -> [View002]
  Rotation = 0
  ScaleType = 0
  TheoreticalExact = false
  Type = 2
  UnderTolerance = 0
  X = -64.6748
  Y = -0.853659
FEATURE [TechDraw::DrawViewDimension] Dimension028
  Arbitrary = false
  ArbitraryTolerances = false
  EqualTolerance = true
  FormatSpec = %.2f
  FormatSpecOverTolerance = %+.2f
  FormatSpecUnderTolerance = %+.2f
  Inverted = false
  LockPosition = false
  MeasureType = 1
  OverTolerance = 0
  References2D = -> [View002]
  Rotation = 0
  ScaleType = 0
  TheoreticalExact = false
  Type = 1
  UnderTolerance = 0
  X = 0.284553
  Y = 22.7622
FEATURE [TechDraw::DrawViewDimension] Dimension029
  Arbitrary = false
  ArbitraryTolerances = false
  EqualTolerance = true
  FormatSpec = %.2f
  FormatSpecOverTolerance = %+.2f
  FormatSpecUnderTolerance = %+.2f
  Inverted = false
  LockPosition = false
  MeasureType = 1
  OverTolerance = 0
  References2D = -> [View002]
  Rotation = 0
  ScaleType = 0
  TheoreticalExact = false
  Type = 2
  UnderTolerance = 0
  X = -17.0711
  Y = 0.853659
FEATURE [TechDraw::DrawViewDimension] Dimension030
  Arbitrary = false
  ArbitraryTolerances = false
  EqualTolerance = true
  FormatSpec = %.2f
  FormatSpecOverTolerance = %+.2f
  FormatSpecUnderTolerance = %+.2f
  Inverted = false
  LockPosition = false
  MeasureType = 1
  OverTolerance = 0
  References2D = -> [View002]
  Rotation = 0
  ScaleType = 0
  TheoreticalExact = false
  Type = 1
  UnderTolerance = 0
  X = 0.853659
  Y = -28.3333
FEATURE [TechDraw::DrawViewDimension] Dimension031
  Arbitrary = false
  ArbitraryTolerances = false
  EqualTolerance = true
  FormatSpec = %.2f
  FormatSpecOverTolerance = %+.2f
  FormatSpecUnderTolerance = %+.2f
  Inverted = false
  LockPosition = false
  MeasureType = 1
  OverTolerance = 0
  References2D = -> [View002]
  Rotation = 0
  ScaleType = 0
  TheoreticalExact = false
  Type = 1
  UnderTolerance = 0
  X = 0
  Y = -45
FEATURE [TechDraw::DrawViewDimension] Dimension032
  Arbitrary = false
  ArbitraryTolerances = false
  EqualTolerance = true
  FormatSpec = %.2f
  FormatSpecOverTolerance = %+.2f
  FormatSpecUnderTolerance = %+.2f
  Inverted = false
  LockPosition = false
  MeasureType = 1
  OverTolerance = 0
  References2D = -> [View002]
  Rotation = 0
  ScaleType = 0
  TheoreticalExact = false
  Type = 2
  UnderTolerance = 0
  X = 65.8943
  Y = -1.42276
FEATURE [TechDraw::DrawViewDimension] Dimension033
  Arbitrary = false
  ArbitraryTolerances = false
  EqualTolerance = true
  FormatSpec = %.2f
  FormatSpecOverTolerance = %+.2f
  FormatSpecUnderTolerance = %+.2f
  Inverted = false
  LockPosition = false
  MeasureType = 1
  OverTolerance = 0
  References2D = -> [View002]
  Rotation = 0
  ScaleType = 0
  TheoreticalExact = false
  Type = 2
  UnderTolerance = 0
  X = 75.7317
  Y = -2.56098
FEATURE [TechDraw::DrawViewDimension] Dimension034
  Arbitrary = false
  ArbitraryTolerances = false
  EqualTolerance = true
  FormatSpec = %.2f
  FormatSpecOverTolerance = %+.2f
  FormatSpecUnderTolerance = %+.2f
  Inverted = false
  LockPosition = false
  MeasureType = 1
  OverTolerance = 0
  References2D = -> [View002]
  Rotation = 0
  ScaleType = 0
  TheoreticalExact = false
  Type = 1
  UnderTolerance = 0
  X = 24.125
  Y = 24.125
FEATURE [TechDraw::DrawViewDimension] Dimension035
  Arbitrary = false
  ArbitraryTolerances = false
  EqualTolerance = true
  FormatSpec = %.2f
  FormatSpecOverTolerance = %+.2f
  FormatSpecUnderTolerance = %+.2f
  Inverted = false
  LockPosition = false
  MeasureType = 1
  OverTolerance = 0
  References2D = -> [View002]
  Rotation = 0
  ScaleType = 0
  TheoreticalExact = false
  Type = 2
  UnderTolerance = 0
  X = 24.125
  Y = -24.125
FEATURE [TechDraw::DrawViewAnnotation] Annotation002
  Font = osifont
  LineSpace = 80
  LockPosition = false
  MaxWidth = -1
  Rotation = 0
  ScaleType = 0
  Text = Lochdurchmesser: 3mm
  TextSize = 5
  TextStyle = 0
  X = 70.5325
  Y = 45.813
FEATURE [TechDraw::DrawViewAnnotation] Annotation003
  Font = osifont
  LineSpace = 80
  LockPosition = false
  MaxWidth = -1
  Rotation = 0
  ScaleType = 0
  Text = Aludicke: 2mm
  TextSize = 5
  TextStyle = 0
  X = 120.898
  Y = 47.8049
FEATURE [TechDraw::DrawPage] Page002  label="Fixierungsplatte_Sk"
  KeepUpdated = true
  NextBalloonIndex = 1
  ProjectionType = 0
  Template = -> Template002
  Views = -> [View002,Dimension026,Dimension027,Dimension028,Dimension029,Dimension030,Dimension031,Dimension032,Dimension033,Dimension034,Dimension035,Annotation002,Annotation003]
